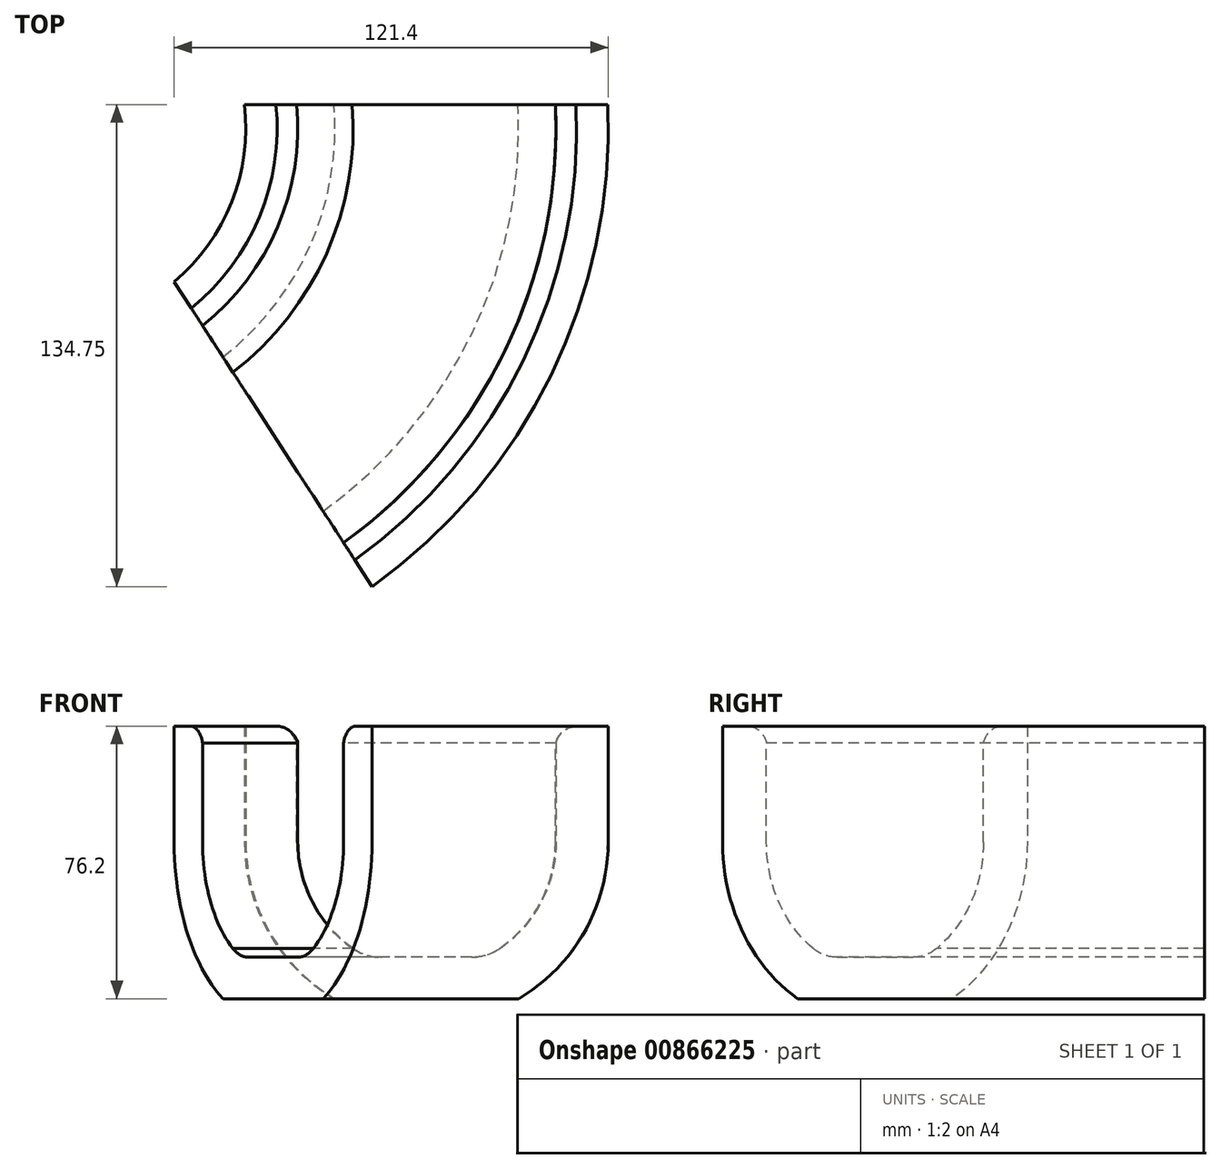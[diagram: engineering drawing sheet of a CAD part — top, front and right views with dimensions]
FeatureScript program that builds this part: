
annotation { "Feature Type Name" : "Feature", "Feature Type Description" : "" }
export const myFeature = defineFeature(function(context is Context, id is Id, definition is map)
    precondition{}
    {
        {
            var Q0;
            Q0=qCreatedBy(makeId("Front.planeOp"),FACE);
            var sketch = newSketch(context, id + "F0", { "sketchPlane" : qUnion([Q0])});
            skArc(sketch, "E0", {"start": v(-36.19, 0) * mm, "mid": v(-32.07, -16.77) * mm, "end": v(-20.64, -29.72) * mm});
            skLineSegment(sketch, "E1", {"start": v(-12.67, -32.22) * mm, "end": v(0, -32.22) * mm});
            skLineSegment(sketch, "E2.top", {"start": v(-25.73, -43.8) * mm, "end": v(0, -43.8) * mm});
            skLineSegment(sketch, "E2.left", {"start": v(-50.8, 32.4) * mm, "end": v(-50.8, 0) * mm});
            skLineSegment(sketch, "E3", {"start": v(-36.19, 0) * mm, "end": v(-36.19, 27.7) * mm});
            skLineSegment(sketch, "E4", {"start": v(-41.98, 32.4) * mm, "end": v(-50.8, 32.4) * mm});
            skArc(sketch, "E5", {"start": v(-36.19, 27.7) * mm, "mid": v(-38.34, 30.97) * mm, "end": v(-41.98, 32.4) * mm});
            skLineSegment(sketch, "E6", {"start": v(0, -32.22) * mm, "end": v(0, -43.8) * mm, "construction": true});
            skPoint(sketch, "E7.visualSharp", {"position": v(-16.48, -32.22) * mm});
            skArc(sketch, "E7.filletArc", {"start": v(-20.64, -29.72) * mm, "mid": v(-16.85, -31.58) * mm, "end": v(-12.67, -32.22) * mm});
            skArc(sketch, "E8.MirrorCS", {"start": v(20.64, -29.72) * mm, "mid": v(16.85, -31.58) * mm, "end": v(12.67, -32.22) * mm});
            skArc(sketch, "E9.MirrorCS", {"start": v(36.19, 27.7) * mm, "mid": v(38.34, 30.97) * mm, "end": v(41.98, 32.4) * mm});
            skLineSegment(sketch, "E10.MirrorCS", {"start": v(41.98, 32.4) * mm, "end": v(50.8, 32.4) * mm});
            skArc(sketch, "E11.MirrorCS", {"start": v(36.19, 0) * mm, "mid": v(32.07, -16.77) * mm, "end": v(20.64, -29.72) * mm});
            skLineSegment(sketch, "E12.MirrorCS", {"start": v(25.73, -43.8) * mm, "end": v(0, -43.8) * mm});
            skLineSegment(sketch, "E13.MirrorCS", {"start": v(12.67, -32.22) * mm, "end": v(0, -32.22) * mm});
            skPoint(sketch, "E14.MirrorP", {"position": v(16.48, -32.22) * mm});
            skLineSegment(sketch, "E15.MirrorCS", {"start": v(36.19, 0) * mm, "end": v(36.19, 27.7) * mm});
            skLineSegment(sketch, "E16.MirrorCS", {"start": v(50.8, 32.4) * mm, "end": v(50.8, 0) * mm});
            skArc(sketch, "E17", {"start": v(-50.8, 0) * mm, "mid": v(-44.09, -25.24) * mm, "end": v(-25.73, -43.8) * mm});
            skArc(sketch, "E18.trimOffspring", {"start": v(25.73, -43.8) * mm, "mid": v(44.09, -25.24) * mm, "end": v(50.8, 0) * mm});
            skSolve(sketch);
        }
        {
            var Q0;
            Q0=qCreatedBy(makeId("Top.planeOp"),FACE);
            var sketch = newSketch(context, id + "F1", { "sketchPlane" : qUnion([Q0])});
            skArc(sketch, "E19", {"start": v(-42.78, -92.16) * mm, "mid": v(-9.7, -51.5) * mm, "end": v(0, 0) * mm});
            skSolve(sketch);
        }
        {
            var Q0;
            Q0=makeQuery(id+"F0.imprint","IMPRINT",FACE,{"disambiguationData":[TD([[makeQuery(id+"F0.imprint","IMPRINT",EDGE,{"derivedFrom":sQuery(id+"F0.wireOp",EDGE,"E0")}),-1.0]])]});
            var Q1;
            Q1=sQuery(id+"F1.wireOp",EDGE,"E19");
            sweep(context, id + "F2", {"profiles" : qUnion([Q0]), "path" : qUnion([Q1])});
        }
    });
